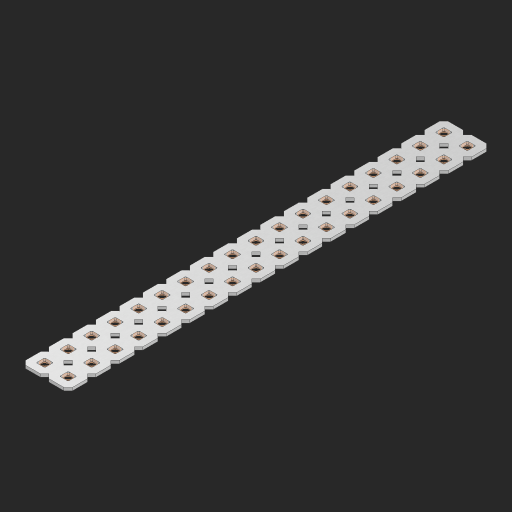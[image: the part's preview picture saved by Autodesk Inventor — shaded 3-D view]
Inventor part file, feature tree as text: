
AUTODESK INVENTOR PART (.ipt)
format: ipt  version: 2023 (Build 270158000, 158)  size: 688,128 bytes
history: native  units: in
note: dims shown in document units (in); Inventor stores cm internally (conversion verified against a paired STEP export)
features: other x37, extrude x35, sketch x2, pattern_linear x1
ambient origin geometry x8: Origin, YZ Plane, XZ Plane, XY Plane, X Axis, Y Axis, Z Axis, Center Point
bodies: Solid1 (feature_tree), Body (feature_tree)
feature tree (75):
  pattern_linear  "Rectangular Pattern1"  Spacing1=0.09in  [1 undecoded]
  sketch  "Sketch1"  dims[d1=0.5in]
  sketch  "Sketch2"  dims[d2=0.182in d3=0.09in d4=0.09in d5=0.09in d6=0.09in d7=0.09in d8=0.09in d9=0.09in d10=0.09in d11=0.02in d13=0.0in d14=0.172in d15=0.0625in d16=0.0in d19=0.5in d22=0.5in]
  other  "Srf1"
  other  "Srf126"
  other  "Srf127"
  other  "Srf128"
  other  "Srf129"
  other  "Srf130"
  other  "Srf131"
  other  "Srf250"
  other  "Srf251"
  other  "Srf252"
  other  "Srf253"
  other  "Srf254"
  other  "Srf255"
  other  "Srf256"
  other  "Srf257"
  other  "Srf258"
  other  "Srf259"
  other  "Srf260"
  other  "Srf268"
  other  "Srf269"
  other  "Srf270"
  other  "Srf271"
  other  "Srf272"
  other  "Srf273"
  other  "Srf274"
  other  "Srf275"
  other  "Srf276"
  other  "Srf277"
  other  "Srf278"
  other  "Srf279"
  other  "Srf280"
  other  "Srf281"
  other  "Srf282"
  other  "Srf283"
  other  "Srf284"
  other  "Srf285"
  other  "Circle"
  extrude  "ExtrusionSrf126"  Depth=0.09in
  extrude  "ExtrusionSrf127"  Depth=0.09in
  extrude  "ExtrusionSrf128"  Depth=0.09in
  extrude  "ExtrusionSrf129"  Depth=0.09in
  extrude  "ExtrusionSrf130"  Depth=0.09in
  extrude  "ExtrusionSrf131"  Depth=0.09in
  extrude  "ExtrusionSrf250"  Depth=0.09in
  extrude  "ExtrusionSrf251"  Depth=0.02in
  extrude  "ExtrusionSrf252"  TaperAngle=0.0deg  [1 undecoded]
  extrude  "ExtrusionSrf253"  Depth=0.5in
  extrude  "ExtrusionSrf254"  Depth=0.0625in TaperAngle=0.0deg
  extrude  "ExtrusionSrf255"  Depth=0.5in
  extrude  "ExtrusionSrf256"  Depth=0.5in
  extrude  "ExtrusionSrf257"  [1 undecoded]
  extrude  "ExtrusionSrf258"  [1 undecoded]
  extrude  "ExtrusionSrf259"  [1 undecoded]
  extrude  "ExtrusionSrf260"  [1 undecoded]
  extrude  "ExtrusionSrf268"  [1 undecoded]
  extrude  "ExtrusionSrf269"  [1 undecoded]
  extrude  "ExtrusionSrf270"  [1 undecoded]
  extrude  "ExtrusionSrf271"  [1 undecoded]
  extrude  "ExtrusionSrf272"  [1 undecoded]
  extrude  "ExtrusionSrf273"  [1 undecoded]
  extrude  "ExtrusionSrf274"  [1 undecoded]
  extrude  "ExtrusionSrf275"  [1 undecoded]
  extrude  "ExtrusionSrf276"  [1 undecoded]
  extrude  "ExtrusionSrf277"  [1 undecoded]
  extrude  "ExtrusionSrf278"  [1 undecoded]
  extrude  "ExtrusionSrf279"  [1 undecoded]
  extrude  "ExtrusionSrf280"  [1 undecoded]
  extrude  "ExtrusionSrf281"  [1 undecoded]
  extrude  "ExtrusionSrf282"  [1 undecoded]
  extrude  "ExtrusionSrf283"  [1 undecoded]
  extrude  "ExtrusionSrf284"  [1 undecoded]
  extrude  "ExtrusionSrf285"  [1 undecoded]
note: 24 required parameter values undecoded (feature->parameter linkage not recoverable at this tier; creation-order binding heuristic only, values carry confidence <= 0.55)
